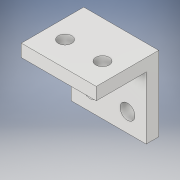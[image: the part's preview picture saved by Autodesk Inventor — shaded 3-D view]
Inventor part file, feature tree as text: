
AUTODESK INVENTOR PART (.ipt)
format: ipt  version: 2017 (Build 210142000, 142)  size: 126,976 bytes
history: native  units: in
note: dims shown in document units (in); Inventor stores cm internally (conversion verified against a paired STEP export)
features: sketch x3, hole x2, projected_geometry x2, extrude x1
ambient origin geometry x8: Origin, YZ Plane, XZ Plane, XY Plane, X Axis, Y Axis, Z Axis, Center Point
bodies: Solid1 (feature_tree)
feature tree (8):
  extrude  "Extrusion1"  Depth=0.625in
  hole  "Hole1"  [1 undecoded]
  hole  "Hole2"  [1 undecoded]
  sketch  "Sketch1"  dims[d0=0.75in d1=0.625in]
  sketch  "Sketch2"  dims[d2=0.625in d3=0.5in]
  projected_geometry  "Projected Loop1"
  sketch  "Sketch3"  dims[d4=0.75in d5=0.0in d6=0.375in d7=0.1875in d8=0.625in d11=0.135in d12=0.75in d13=0.375in d14=0.25in d15=0.5635in d16=1.0in d17=0.8108in d18=0.375in d19=0.375in d20=0.375in d21=0.1875in d22=0.1875in d23=0.1875in d24=0.15in d25=0.75in d26=0.375in d27=0.25in d28=0.5635in d29=1.0in d30=0.8108in d31=0.75in d32=0.75in]
  projected_geometry  "Projected Loop2"
note: 2 required parameter values undecoded (feature->parameter linkage not recoverable at this tier; creation-order binding heuristic only, values carry confidence <= 0.55)
